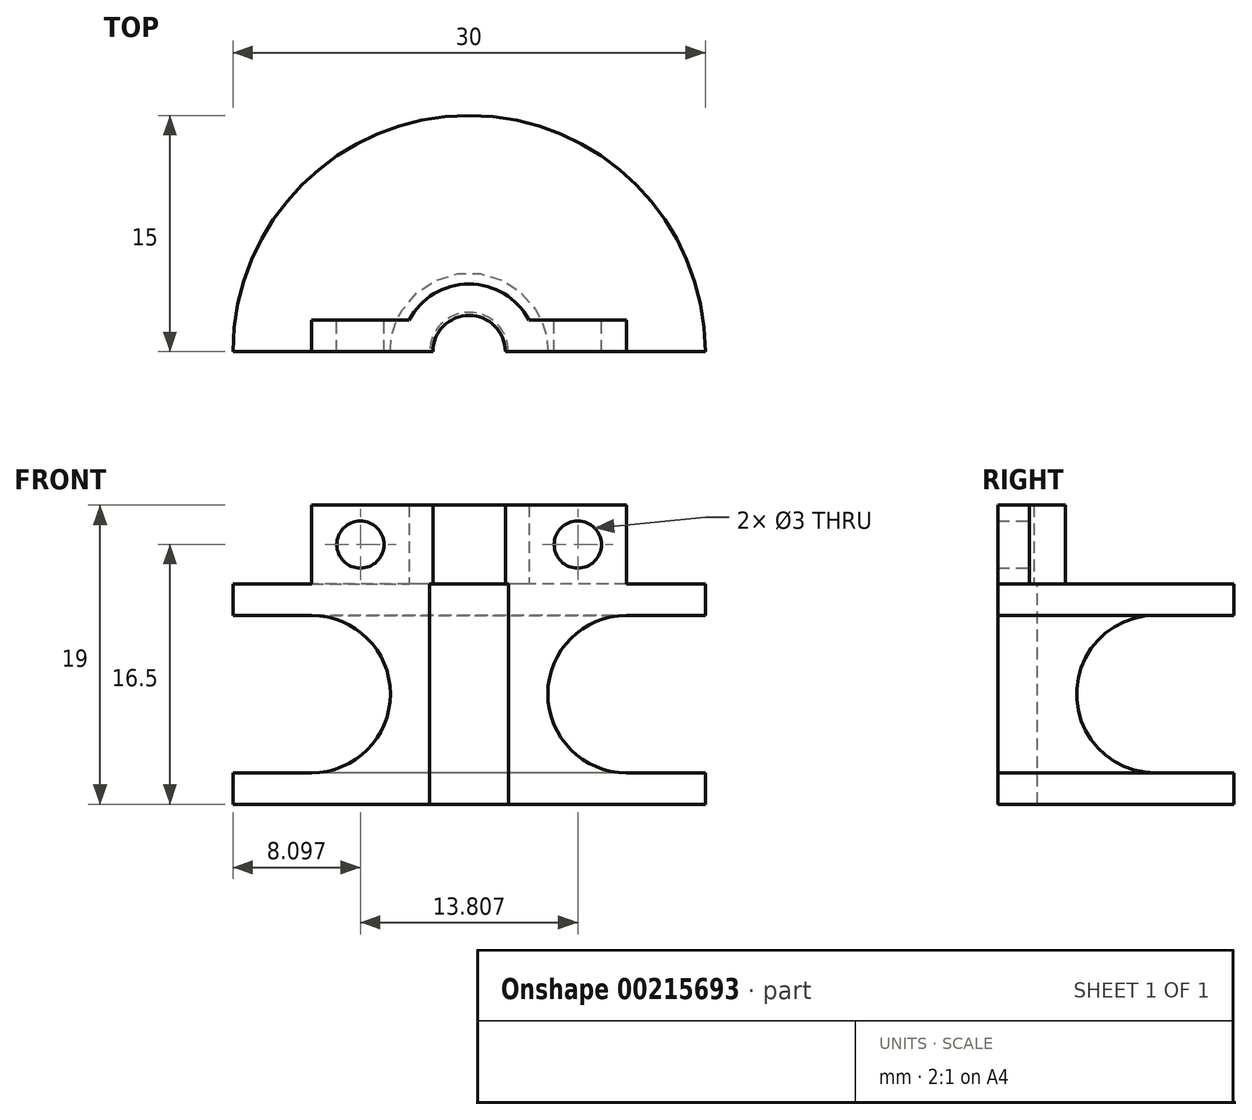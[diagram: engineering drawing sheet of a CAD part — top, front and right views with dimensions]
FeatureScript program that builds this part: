
annotation { "Feature Type Name" : "Feature", "Feature Type Description" : "" }
export const myFeature = defineFeature(function(context is Context, id is Id, definition is map)
    precondition{}
    {
        {
            var Q0;
            Q0=qCreatedBy(makeId("Front.planeOp"),FACE);
            var sketch = newSketch(context, id + "F0", { "sketchPlane" : qUnion([Q0])});
            skLineSegment(sketch, "E0", {"start": v(0, 20.83) * mm, "end": v(0, -19.48) * mm, "construction": true});
            skLineSegment(sketch, "E1", {"start": v(-2.5, 7) * mm, "end": v(-15, 7) * mm});
            skLineSegment(sketch, "E2", {"start": v(-15, 7) * mm, "end": v(-15, 5) * mm});
            skLineSegment(sketch, "E3", {"start": v(-15, 5) * mm, "end": v(-5, 5) * mm});
            skLineSegment(sketch, "E4", {"start": v(-5, 5) * mm, "end": v(-5, -5) * mm});
            skLineSegment(sketch, "E5", {"start": v(-5, -5) * mm, "end": v(-15, -5) * mm});
            skLineSegment(sketch, "E6", {"start": v(-15, -5) * mm, "end": v(-15, -7) * mm});
            skLineSegment(sketch, "E7", {"start": v(-15, -7) * mm, "end": v(-2.5, -7) * mm});
            skLineSegment(sketch, "E8", {"start": v(-2.5, -7) * mm, "end": v(-2.5, 7) * mm});
            skSolve(sketch);
        }
        {
            var Q0;
            Q0 = qSketchRegion(id + "F0", true);
            var Q1;
            Q1=sQuery(id+"F0.wireOp",EDGE,"E0");
            revolve(context, id + "F1", {"entities" : qUnion([Q0]), "axis" : qUnion([Q1]), "revolveType" : RevolveType.ONE_DIRECTION, "angle" : 180 * degree});
        }
        {
            var Q0;
            Q0=makeQuery(id+"F1.opRevolve","SWEPT_FACE",FACE,{"disambiguationData":[OSD([sQuery(id+"F0.wireOp",EDGE,"E1")])]});
            var sketch = newSketch(context, id + "F2", { "sketchPlane" : qUnion([Q0])});
            skLineSegment(sketch, "E9.bottom", {"start": v(-10, 0) * mm, "end": v(-2.3, 0) * mm});
            skLineSegment(sketch, "E9.top", {"start": v(-10, 2) * mm, "end": v(-3.8, 2) * mm});
            skLineSegment(sketch, "E9.left", {"start": v(-10, 0) * mm, "end": v(-10, 2) * mm});
            skLineSegment(sketch, "E10.MirrorCS", {"start": v(10, 2) * mm, "end": v(3.8, 2) * mm});
            skLineSegment(sketch, "E11.MirrorCS", {"start": v(10, 0) * mm, "end": v(10, 2) * mm});
            skLineSegment(sketch, "E12.MirrorCS", {"start": v(10, 0) * mm, "end": v(2.3, 0) * mm});
            skArc(sketch, "E13", {"start": v(3.8, 2) * mm, "mid": v(0, 4.3) * mm, "end": v(-3.8, 2) * mm});
            skArc(sketch, "E14", {"start": v(2.3, 0) * mm, "mid": v(0, 2.3) * mm, "end": v(-2.3, 0) * mm});
            skPoint(sketch, "E9.right.end.orphan", {"position": v(-2.5, 2) * mm});
            skPoint(sketch, "E15.MirrorCS.end.orphan", {"position": v(2.5, 2) * mm});
            skPoint(sketch, "E15.MirrorCS.start.orphan", {"position": v(2.3, 0) * mm});
            skSolve(sketch);
        }
        {
            var Q0;
            Q0 = qSketchRegion(id + "F2", true);
            extrude(context, id + "F3", {"entities" : qUnion([Q0]), "operationType" : NewBodyOperationType.ADD, "depth" : 5 * mm});
        }
        {
            var Q0;
            Q0=makeQuery(id+"F3.opExtrude","SWEPT_FACE",FACE,{"disambiguationData":[OSD([sQuery(id+"F2.wireOp",EDGE,"E9.top")])]});
            var sketch = newSketch(context, id + "F4", { "sketchPlane" : qUnion([Q0])});
            skCircle(sketch, "E16", {"center": v(6.9, 9.5) * mm, "radius": 1.5 * mm});
            skPoint(sketch, "E16.centerSnap0", {"position": v(10, 9.5) * mm});
            skPoint(sketch, "E16.centerSnap1", {"position": v(6.9, 12) * mm});
            skCircle(sketch, "E17.MirrorC", {"center": v(-6.9, 9.5) * mm, "radius": 1.5 * mm});
            skSolve(sketch);
        }
        {
            var Q0;
            Q0 = qSketchRegion(id + "F4", true);
            extrude(context, id + "F5", {"entities" : qUnion([Q0]), "operationType" : NewBodyOperationType.REMOVE, "endBound" : BoundingType.THROUGH_ALL, "oppositeDirection" : true, "depth" : 25 * mm});
        }
        {
            var Q0;
            Q0=makeQuery(id+"F1.opRevolve","SWEPT_EDGE",EDGE,{"disambiguationData":[OSD([sQuery(id+"F0.wireOp",EDGE,"E3"),sQuery(id+"F0.wireOp",EDGE,"E4")])]});
            var Q1;
            Q1=makeQuery(id+"F1.opRevolve","SWEPT_EDGE",EDGE,{"disambiguationData":[OSD([sQuery(id+"F0.wireOp",EDGE,"E4"),sQuery(id+"F0.wireOp",EDGE,"E5")])]});
            fillet(context, id + "F6", {"entities" : qUnion([Q0, Q1]), "radius" : 5 * mm, "tangentPropagation" : true, "allowEdgeOverflow" : false});
        }
    });
